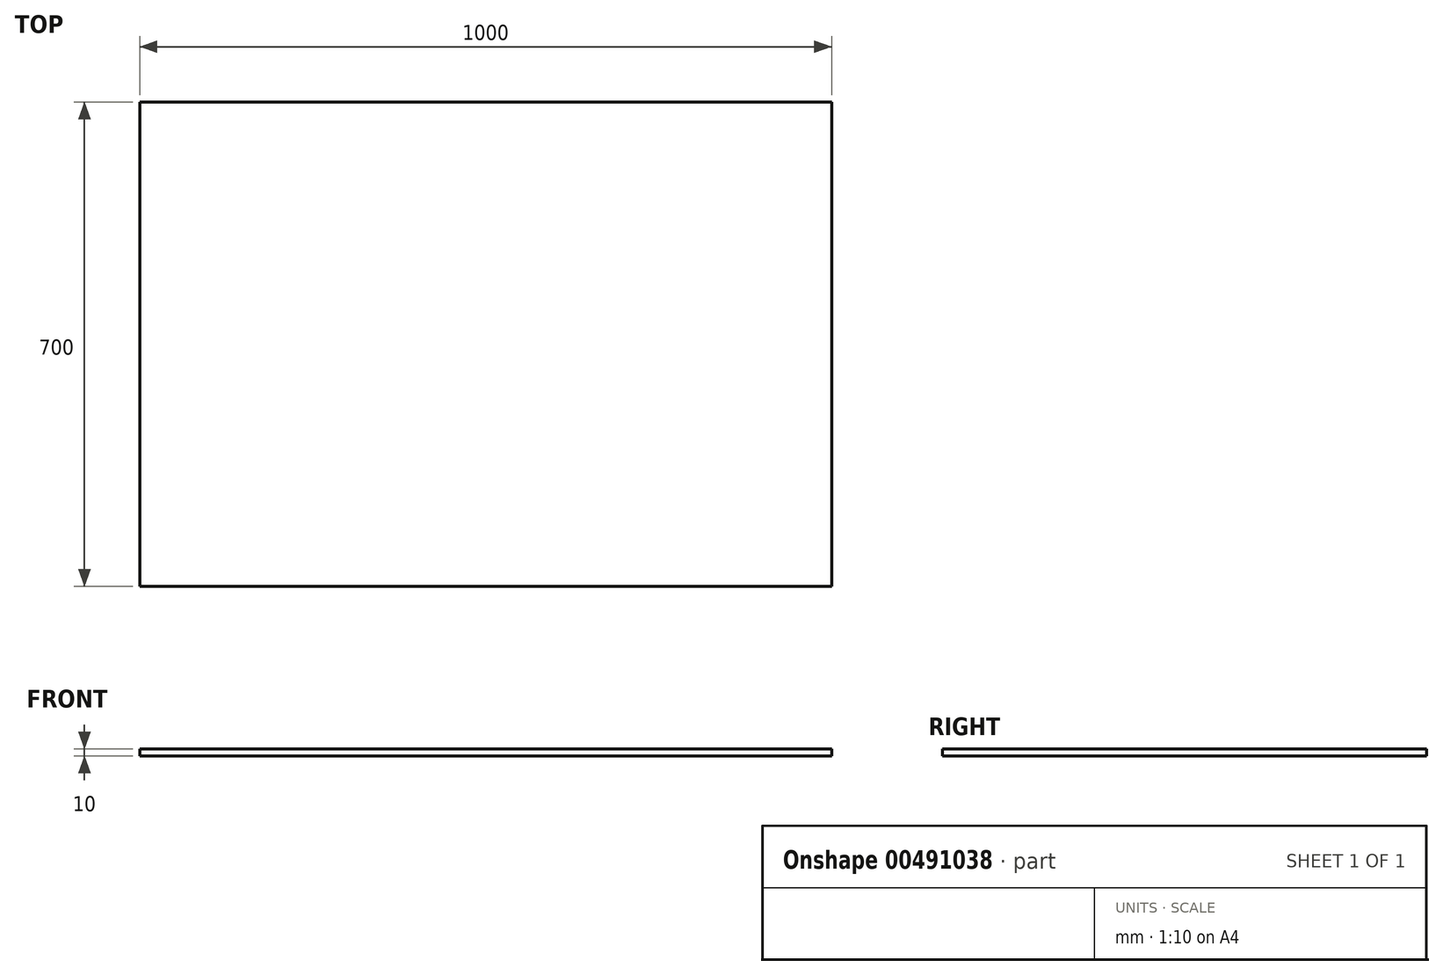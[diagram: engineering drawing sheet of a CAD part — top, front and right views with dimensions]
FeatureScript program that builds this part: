
annotation { "Feature Type Name" : "Feature", "Feature Type Description" : "" }
export const myFeature = defineFeature(function(context is Context, id is Id, definition is map)
    precondition{}
    {
        {
            var Q0;
            Q0=qCreatedBy(makeId("Top.planeOp"),FACE);
            var sketch = newSketch(context, id + "F0", { "sketchPlane" : qUnion([Q0])});
            skLineSegment(sketch, "E0.bottom", {"start": v(0, 0) * mm, "end": v(1000, 0) * mm});
            skLineSegment(sketch, "E0.top", {"start": v(0, 700) * mm, "end": v(1000, 700) * mm});
            skLineSegment(sketch, "E0.left", {"start": v(0, 0) * mm, "end": v(0, 700) * mm});
            skLineSegment(sketch, "E0.right", {"start": v(1000, 0) * mm, "end": v(1000, 700) * mm});
            skSolve(sketch);
        }
        {
            var Q0;
            Q0 = qSketchRegion(id + "F0", true);
            extrude(context, id + "F1", {"entities" : qUnion([Q0]), "depth" : 10 * mm});
        }
    });
